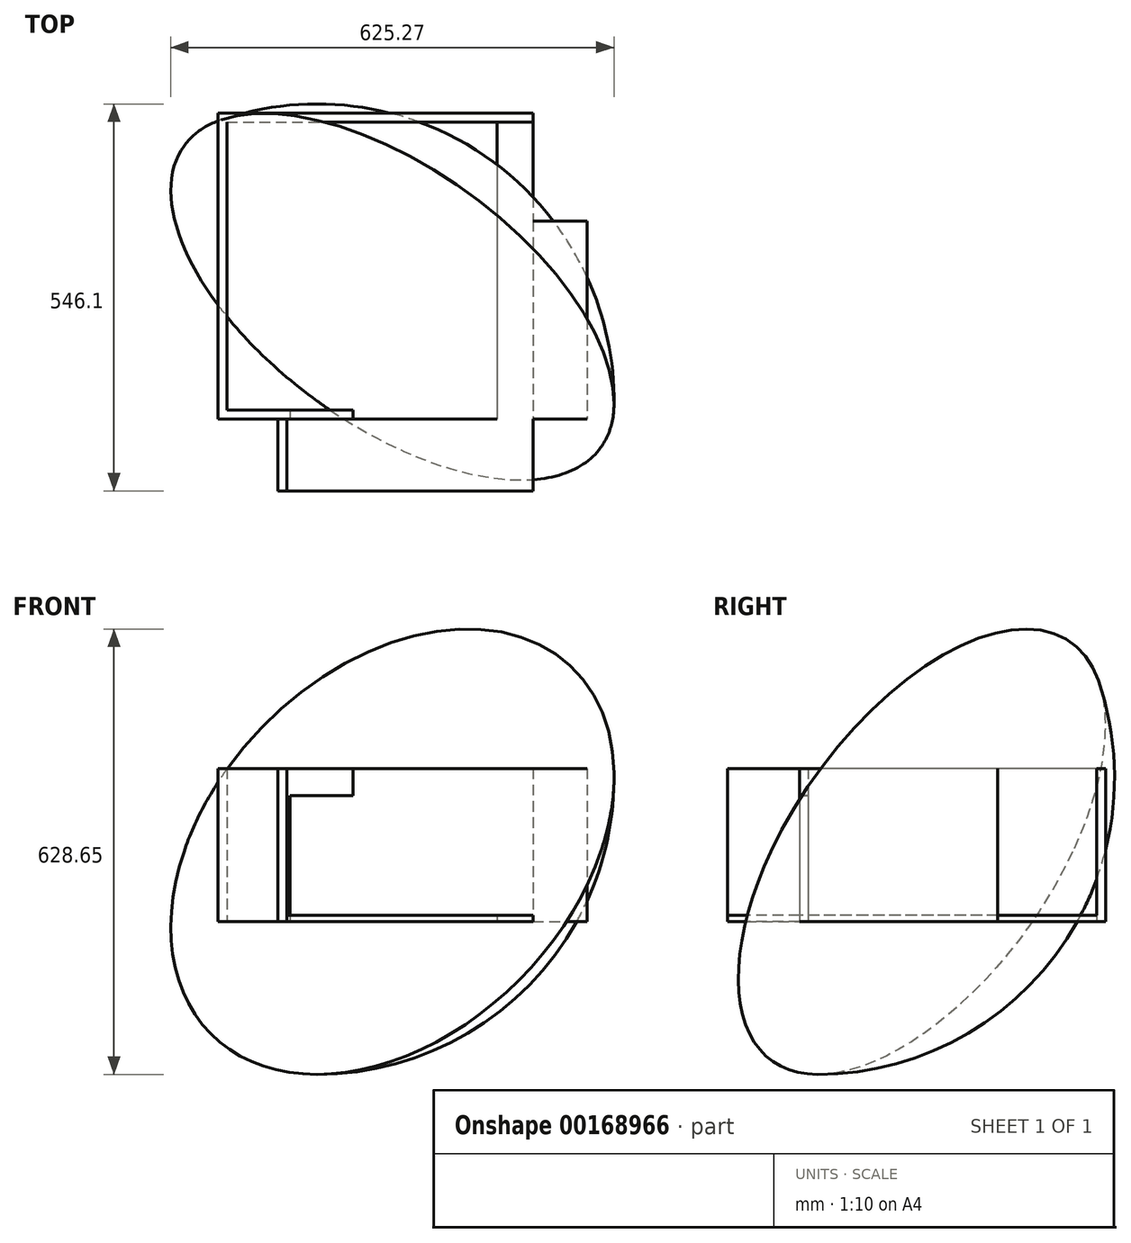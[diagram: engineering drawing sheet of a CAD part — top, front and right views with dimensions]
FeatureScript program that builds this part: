
annotation { "Feature Type Name" : "Feature", "Feature Type Description" : "" }
export const myFeature = defineFeature(function(context is Context, id is Id, definition is map)
    precondition{}
    {
        {
            var Q0;
            Q0=qCreatedBy(makeId("Top.planeOp"),FACE);
            var sketch = newSketch(context, id + "F0", { "sketchPlane" : qUnion([Q0])});
            skLineSegment(sketch, "E0.bottom", {"start": v(190.5, 209.55) * mm, "end": v(-190.5, 209.55) * mm});
            skLineSegment(sketch, "E0.top", {"start": v(190.5, -209.55) * mm, "end": v(-190.5, -209.55) * mm});
            skLineSegment(sketch, "E0.left", {"start": v(190.5, 209.55) * mm, "end": v(190.5, -209.55) * mm});
            skLineSegment(sketch, "E0.right", {"start": v(-190.5, 209.55) * mm, "end": v(-190.5, -209.55) * mm});
            skPoint(sketch, "E0.middle", {"position": v(0, 0) * mm});
            skLineSegment(sketch, "E1.bottom", {"start": v(190.5, 209.55) * mm, "end": v(241.3, 209.55) * mm});
            skLineSegment(sketch, "E1.top", {"start": v(190.5, -209.55) * mm, "end": v(241.3, -209.55) * mm});
            skLineSegment(sketch, "E1.right", {"start": v(241.3, 209.55) * mm, "end": v(241.3, -209.55) * mm});
            skLineSegment(sketch, "E2.top", {"start": v(190.5, 158.75) * mm, "end": v(-190.5, 158.75) * mm});
            skLineSegment(sketch, "E2.left", {"start": v(190.5, 209.55) * mm, "end": v(190.5, 158.75) * mm});
            skLineSegment(sketch, "E2.right", {"start": v(-190.5, 209.55) * mm, "end": v(-190.5, 158.75) * mm});
            skLineSegment(sketch, "E3.bottom", {"start": v(-190.5, -209.55) * mm, "end": v(-63.5, -209.55) * mm});
            skLineSegment(sketch, "E3.top", {"start": v(-190.5, 158.75) * mm, "end": v(-63.5, 158.75) * mm});
            skLineSegment(sketch, "E3.left", {"start": v(-190.5, -209.55) * mm, "end": v(-190.5, 158.75) * mm});
            skLineSegment(sketch, "E3.right", {"start": v(-63.5, -209.55) * mm, "end": v(-63.5, 158.75) * mm});
            skLineSegment(sketch, "E4.bottom", {"start": v(114.3, -209.55) * mm, "end": v(-63.5, -209.55) * mm});
            skLineSegment(sketch, "E4.top", {"start": v(114.3, -133.35) * mm, "end": v(-63.5, -133.35) * mm});
            skLineSegment(sketch, "E4.left", {"start": v(114.3, -209.55) * mm, "end": v(114.3, -133.35) * mm});
            skLineSegment(sketch, "E4.right", {"start": v(-63.5, -209.55) * mm, "end": v(-63.5, -133.35) * mm});
            skLineSegment(sketch, "E5.bottom", {"start": v(-190.5, -209.55) * mm, "end": v(-12.7, -209.55) * mm});
            skLineSegment(sketch, "E5.top", {"start": v(-190.5, -196.85) * mm, "end": v(-12.7, -196.85) * mm});
            skLineSegment(sketch, "E5.left", {"start": v(-190.5, -209.55) * mm, "end": v(-190.5, -196.85) * mm});
            skLineSegment(sketch, "E5.right", {"start": v(-12.7, -209.55) * mm, "end": v(-12.7, -196.85) * mm});
            skLineSegment(sketch, "E6.bottom", {"start": v(241.3, 69.85) * mm, "end": v(317.5, 69.85) * mm});
            skLineSegment(sketch, "E6.top", {"start": v(241.3, -209.55) * mm, "end": v(317.5, -209.55) * mm});
            skLineSegment(sketch, "E6.left", {"start": v(241.3, 69.85) * mm, "end": v(241.3, -209.55) * mm});
            skLineSegment(sketch, "E6.right", {"start": v(317.5, 69.85) * mm, "end": v(317.5, -209.55) * mm});
            skLineSegment(sketch, "E7", {"start": v(-59.05, 209.55) * mm, "end": v(-59.05, 196.85) * mm});
            skLineSegment(sketch, "E8", {"start": v(241.3, -107.95) * mm, "end": v(228.6, -107.95) * mm});
            skLineSegment(sketch, "E9", {"start": v(-59.05, 196.85) * mm, "end": v(228.6, -107.95) * mm});
            skArc(sketch, "E10", {"start": v(265.13, 309.56) * mm, "mid": v(-114.7, 132.44) * mm, "end": v(-151.23, -285.07) * mm, "construction": true});
            skLineSegment(sketch, "E11", {"start": v(228.6, -107.95) * mm, "end": v(-151.23, -285.07) * mm, "construction": true});
            skLineSegment(sketch, "E12", {"start": v(228.6, -107.95) * mm, "end": v(265.13, 309.56) * mm, "construction": true});
            skArc(sketch, "E13", {"start": v(-217.2, -191.26) * mm, "mid": v(197.99, -134.17) * mm, "end": v(356.14, 253.94) * mm, "construction": true});
            skLineSegment(sketch, "E14", {"start": v(-59.05, 196.85) * mm, "end": v(-217.2, -191.26) * mm, "construction": true});
            skLineSegment(sketch, "E15", {"start": v(-59.05, 196.85) * mm, "end": v(356.14, 253.94) * mm, "construction": true});
            skLineSegment(sketch, "E16", {"start": v(-63.5, -196.85) * mm, "end": v(-63.5, -184.15) * mm});
            skLineSegment(sketch, "E17", {"start": v(-63.5, -184.15) * mm, "end": v(189.23, 196.85) * mm});
            skPoint(sketch, "E17.endSnap0", {"position": v(190.5, 184.15) * mm});
            skLineSegment(sketch, "E18", {"start": v(189.23, 196.85) * mm, "end": v(189.23, 209.55) * mm});
            skArc(sketch, "E19", {"start": v(353.37, -227.35) * mm, "mid": v(182.35, 155.27) * mm, "end": v(-234.52, 198.47) * mm, "construction": true});
            skLineSegment(sketch, "E20", {"start": v(-63.5, -184.15) * mm, "end": v(-234.52, 198.47) * mm, "construction": true});
            skLineSegment(sketch, "E21", {"start": v(-63.5, -184.15) * mm, "end": v(353.37, -227.35) * mm, "construction": true});
            skArc(sketch, "E22", {"start": v(-223.5, 269.63) * mm, "mid": v(-70.56, -132.02) * mm, "end": v(355.58, -187.82) * mm, "construction": true});
            skLineSegment(sketch, "E23", {"start": v(189.23, 196.85) * mm, "end": v(332.57, -196.98) * mm, "construction": true});
            skLineSegment(sketch, "E24", {"start": v(189.23, 196.85) * mm, "end": v(-223.5, 269.63) * mm, "construction": true});
            skSolve(sketch);
        }
        {
            var Q0;
            Q0=qCreatedBy(makeId("Top.planeOp"),FACE);
            var sketch = newSketch(context, id + "F1", { "sketchPlane" : qUnion([Q0])});
            skLineSegment(sketch, "E25.0", {"start": v(190.5, 209.55) * mm, "end": v(241.3, 209.55) * mm});
            skLineSegment(sketch, "E26.0", {"start": v(190.5, 209.55) * mm, "end": v(-190.5, 209.55) * mm});
            skLineSegment(sketch, "E27.0", {"start": v(-190.5, 209.55) * mm, "end": v(-190.5, 158.75) * mm});
            skLineSegment(sketch, "E28.0", {"start": v(-190.5, 209.55) * mm, "end": v(-190.5, -197.06) * mm});
            skLineSegment(sketch, "E29.0", {"start": v(190.5, 222.25) * mm, "end": v(241.3, 222.25) * mm});
            skLineSegment(sketch, "E29.1", {"start": v(190.5, 222.25) * mm, "end": v(-203.2, 222.25) * mm});
            skLineSegment(sketch, "E29.2", {"start": v(-203.2, 222.25) * mm, "end": v(-203.2, -209.55) * mm});
            skLineSegment(sketch, "E30", {"start": v(241.3, 209.55) * mm, "end": v(241.3, 222.25) * mm});
            skLineSegment(sketch, "E31", {"start": v(-190.5, -209.55) * mm, "end": v(-203.2, -209.55) * mm});
            skLineSegment(sketch, "E32", {"start": v(-190.5, -197.06) * mm, "end": v(-101.6, -197.06) * mm});
            skLineSegment(sketch, "E33", {"start": v(-101.6, -197.06) * mm, "end": v(-101.6, -209.55) * mm});
            skLineSegment(sketch, "E34", {"start": v(-101.6, -209.55) * mm, "end": v(-190.5, -209.55) * mm});
            skLineSegment(sketch, "E35.0", {"start": v(241.3, 69.85) * mm, "end": v(317.5, 69.85) * mm});
            skLineSegment(sketch, "E36.0", {"start": v(317.5, 69.85) * mm, "end": v(317.5, -209.55) * mm});
            skLineSegment(sketch, "E37.0", {"start": v(241.3, -209.55) * mm, "end": v(317.5, -209.55) * mm});
            skLineSegment(sketch, "E38.0", {"start": v(241.3, 69.85) * mm, "end": v(241.3, -209.55) * mm});
            skPoint(sketch, "E39.orphan", {"position": v(241.3, 209.55) * mm});
            skSolve(sketch);
        }
        {
            var Q0;
            Q0=makeQuery(id+"F1.imprint","IMPRINT",FACE,{"disambiguationData":[TD([[makeQuery(id+"F1.imprint","IMPRINT",EDGE,{"derivedFrom":sQuery(id+"F1.wireOp",EDGE,"E25.0")}),1.0]])]});
            var Q1;
            {var subQ3=sQuery(id+"F0.wireOp",EDGE,"E6.bottom");Q1=makeQuery(id+"F0.imprint","IMPRINT",FACE,{"disambiguationData":[TD([[makeQuery(id+"F0.imprint","IMPRINT",EDGE,{"derivedFrom":subQ3}),-1.0]])]});}
            extrude(context, id + "F2", {"entities" : qUnion([Q0, Q1]), "depth" : 215.9 * mm});
        }
        {
            var Q0;
            Q0=makeQuery(id+"F2.opExtrude","CAP_FACE",FACE,{"disambiguationData":[OSD([sQuery(id+"F1.wireOp",EDGE,"E25.0"),sQuery(id+"F1.wireOp",EDGE,"E26.0"),sQuery(id+"F1.wireOp",EDGE,"E28.0"),sQuery(id+"F1.wireOp",EDGE,"E29.0"),sQuery(id+"F1.wireOp",EDGE,"E29.1"),sQuery(id+"F1.wireOp",EDGE,"E29.2"),sQuery(id+"F1.wireOp",EDGE,"E30"),sQuery(id+"F1.wireOp",EDGE,"E31"),sQuery(id+"F1.wireOp",EDGE,"E32"),sQuery(id+"F1.wireOp",EDGE,"E33"),sQuery(id+"F1.wireOp",EDGE,"E34")])],"isStart":false});
            var sketch = newSketch(context, id + "F3", { "sketchPlane" : qUnion([Q0])});
            skLineSegment(sketch, "E40.0", {"start": v(-12.7, -209.55) * mm, "end": v(-12.7, -196.85) * mm});
            skLineSegment(sketch, "E41.0", {"start": v(-12.7, -209.55) * mm, "end": v(-63.5, -209.55) * mm});
            skLineSegment(sketch, "E42.0", {"start": v(-101.6, -209.55) * mm, "end": v(-12.7, -209.55) * mm});
            skLineSegment(sketch, "E43.0", {"start": v(-101.6, -197.06) * mm, "end": v(-101.6, -209.55) * mm});
            skPoint(sketch, "E44.orphan", {"position": v(-190.5, -209.55) * mm});
            skPoint(sketch, "E45.0.end.orphan", {"position": v(-12.7, -196.85) * mm});
            skPoint(sketch, "E45.0.start.orphan", {"position": v(-190.5, -196.85) * mm});
            skPoint(sketch, "E46.orphan", {"position": v(114.3, -209.55) * mm});
            skLineSegment(sketch, "E47", {"start": v(-101.6, -197.06) * mm, "end": v(-12.7, -196.85) * mm});
            skSolve(sketch);
        }
        {
            var Q0;
            {var subQ0=sQuery(id+"F3.wireOp",EDGE,"E40.0");Q0=makeQuery(id+"F3.imprint","IMPRINT",FACE,{"disambiguationData":[TD([[makeQuery(id+"F3.imprint","IMPRINT",EDGE,{"derivedFrom":subQ0}),1.0]])]});}
            extrude(context, id + "F4", {"entities" : qUnion([Q0]), "operationType" : NewBodyOperationType.ADD, "oppositeDirection" : true, "depth" : 38.1 * mm});
        }
        {
            var Q0;
            Q0=qCreatedBy(makeId("Top.planeOp"),FACE);
            var sketch = newSketch(context, id + "F5", { "sketchPlane" : qUnion([Q0])});
            skLineSegment(sketch, "E48.0", {"start": v(190.5, 209.55) * mm, "end": v(241.3, 209.55) * mm});
            skLineSegment(sketch, "E49.0", {"start": v(190.5, -209.55) * mm, "end": v(241.3, -209.55) * mm});
            skLineSegment(sketch, "E50.0", {"start": v(190.5, 209.55) * mm, "end": v(190.5, -209.55) * mm});
            skLineSegment(sketch, "E51.0", {"start": v(241.3, 209.55) * mm, "end": v(241.3, -209.55) * mm});
            skLineSegment(sketch, "E52.bottom", {"start": v(241.3, -209.55) * mm, "end": v(-105.83, -209.55) * mm});
            skLineSegment(sketch, "E52.top", {"start": v(241.3, -311.15) * mm, "end": v(-105.83, -311.15) * mm});
            skLineSegment(sketch, "E52.left", {"start": v(241.3, -209.55) * mm, "end": v(241.3, -311.15) * mm});
            skLineSegment(sketch, "E52.right", {"start": v(-105.83, -209.55) * mm, "end": v(-105.83, -311.15) * mm});
            skSolve(sketch);
        }
        {
            var Q0;
            Q0=makeQuery(id+"F5.imprint","IMPRINT",FACE,{"disambiguationData":[TD([[makeQuery(id+"F5.imprint","IMPRINT",EDGE,{"derivedFrom":sQuery(id+"F5.wireOp",EDGE,"E52.top")}),-1.0]])]});
            var Q1;
            Q1=makeQuery(id+"F0.imprint","IMPRINT",FACE,{"disambiguationData":[TD([[makeQuery(id+"F0.imprint","IMPRINT",EDGE,{"derivedFrom":sQuery(id+"F0.wireOp",EDGE,"E1.bottom")}),-1.0]])]});
            var Q2;
            {var subQ2=sQuery(id+"F0.wireOp",EDGE,"E1.top");Q2=makeQuery(id+"F0.imprint","IMPRINT",FACE,{"disambiguationData":[TD([[makeQuery(id+"F0.imprint","IMPRINT",EDGE,{"derivedFrom":subQ2}),1.0]])]});}
            extrude(context, id + "F6", {"entities" : qUnion([Q0, Q1, Q2]), "operationType" : NewBodyOperationType.ADD, "depth" : 8.47 * mm});
        }
        {
            var Q0;
            Q0=qCreatedBy(makeId("Top.planeOp"),FACE);
            var sketch = newSketch(context, id + "F7", { "sketchPlane" : qUnion([Q0])});
            skLineSegment(sketch, "E53.0", {"start": v(-105.83, -209.55) * mm, "end": v(-105.83, -311.15) * mm});
            skLineSegment(sketch, "E54.bottom", {"start": v(-105.83, -311.15) * mm, "end": v(-118.53, -311.15) * mm});
            skLineSegment(sketch, "E54.top", {"start": v(-105.83, -209.55) * mm, "end": v(-118.53, -209.55) * mm});
            skLineSegment(sketch, "E54.left", {"start": v(-105.83, -311.15) * mm, "end": v(-105.83, -209.55) * mm});
            skLineSegment(sketch, "E54.right", {"start": v(-118.53, -311.15) * mm, "end": v(-118.53, -209.55) * mm});
            skSolve(sketch);
        }
        {
            var Q0;
            Q0=makeQuery(id+"F7.imprint","IMPRINT",FACE,{"disambiguationData":[TD([[makeQuery(id+"F7.imprint","IMPRINT",EDGE,{"derivedFrom":sQuery(id+"F7.wireOp",EDGE,"E54.bottom")}),-1.0]])]});
            extrude(context, id + "F8", {"entities" : qUnion([Q0]), "depth" : 215.9 * mm});
        }
        {
            var Q0;
            Q0=makeQuery(id+"F4.boolean.opBoolean","MERGE",FACE,{"derivedFrom":[makeQuery(id+"F2.opExtrude","CAP_FACE",FACE,{"disambiguationData":[OSD([sQuery(id+"F1.wireOp",EDGE,"E25.0"),sQuery(id+"F1.wireOp",EDGE,"E26.0"),sQuery(id+"F1.wireOp",EDGE,"E28.0"),sQuery(id+"F1.wireOp",EDGE,"E29.0"),sQuery(id+"F1.wireOp",EDGE,"E29.1"),sQuery(id+"F1.wireOp",EDGE,"E29.2"),sQuery(id+"F1.wireOp",EDGE,"E30"),sQuery(id+"F1.wireOp",EDGE,"E31"),sQuery(id+"F1.wireOp",EDGE,"E32"),sQuery(id+"F1.wireOp",EDGE,"E33"),sQuery(id+"F1.wireOp",EDGE,"E34")])],"isStart":false}),makeQuery(id+"F4.opExtrude","CAP_FACE",FACE,{"disambiguationData":[OSD([sQuery(id+"F3.wireOp",EDGE,"E40.0"),sQuery(id+"F3.wireOp",EDGE,"E42.0"),sQuery(id+"F3.wireOp",EDGE,"E43.0"),sQuery(id+"F3.wireOp",EDGE,"E47")])],"isStart":true})]});
            cPlane(context, id + "F9", {"entities" : qUnion([Q0]), "cplaneType" : CPlaneType.OFFSET, "offset" : 12.7 * mm, "oppositeDirection" : true, "width" : 152.4 * mm, "height" : 152.4 * mm});
        }
        {
            var Q0;
            Q0=qCreatedBy(id+"F9.planeOp",FACE);
            var sketch = newSketch(context, id + "F10", { "sketchPlane" : qUnion([Q0])});
            skLineSegment(sketch, "E55.0", {"start": v(-63.5, -184.15) * mm, "end": v(-234.52, 198.47) * mm});
            skLineSegment(sketch, "E56.0", {"start": v(-63.5, -184.15) * mm, "end": v(353.37, -227.35) * mm});
            skArc(sketch, "E57.0", {"start": v(353.37, -227.35) * mm, "mid": v(182.35, 155.27) * mm, "end": v(-234.52, 198.47) * mm});
            skArc(sketch, "E58.0", {"start": v(-223.5, 269.63) * mm, "mid": v(-80.17, -124.2) * mm, "end": v(332.57, -196.98) * mm});
            skLineSegment(sketch, "E59.0", {"start": v(189.23, 196.85) * mm, "end": v(-223.5, 269.63) * mm});
            skLineSegment(sketch, "E59.1", {"start": v(189.23, 196.85) * mm, "end": v(332.57, -196.98) * mm});
            skPoint(sketch, "E60.orphan", {"position": v(355.58, -187.82) * mm});
            skLineSegment(sketch, "E61", {"start": v(189.23, 196.85) * mm, "end": v(-80.17, -124.2) * mm});
            skLineSegment(sketch, "E62", {"start": v(-63.5, -184.15) * mm, "end": v(182.35, 155.27) * mm});
            skSolve(sketch);
        }
        {
            var Q0;
            Q0=sQuery(id+"F10.wireOp",EDGE,"E57.0");
            cPoint(context, id + "F11", {"entities" : qUnion([Q0]), "parameter" : 0.5});
        }
        {
            var Q0;
            Q0=sQuery(id+"F0.wireOp",VERTEX,"E20.start");
            var Q1;
            Q1=sQuery(id+"F10.wireOp",VERTEX,"E56.0.start");
            var Q2;
            Q2 = qCreatedBy(id + "F11" ,VERTEX);
            cPlane(context, id + "F12", {"entities" : qUnion([Q0, Q1, Q2]), "cplaneType" : CPlaneType.THREE_POINT, "offset" : 0 * mm, "width" : 152.4 * mm, "height" : 152.4 * mm});
        }
        {
            var Q0;
            Q0=qCreatedBy(id+"F12.planeOp",FACE);
            var sketch = newSketch(context, id + "F13", { "sketchPlane" : qUnion([Q0])});
            skPoint(sketch, "E63.0", {"position": v(-186.39, 203.2) * mm});
            skLineSegment(sketch, "E64.0", {"start": v(-186.39, 203.2) * mm, "end": v(232.71, 203.2) * mm});
            skLineSegment(sketch, "E65", {"start": v(-186.39, 203.2) * mm, "end": v(-186.39, -215.9) * mm});
            skArc(sketch, "E66", {"start": v(-186.39, -215.9) * mm, "mid": v(176.56, -6.35) * mm, "end": v(176.56, 412.75) * mm});
            skLineSegment(sketch, "E67", {"start": v(-186.39, 203.2) * mm, "end": v(176.56, 412.75) * mm});
            skLineSegment(sketch, "E68", {"start": v(-186.39, 203.2) * mm, "end": v(176.56, -6.35) * mm});
            skSolve(sketch);
        }
        {
            var Q0;
            {var subQ0=sQuery(id+"F13.wireOp",EDGE,"E65");Q0=makeQuery(id+"F13.imprint","IMPRINT",FACE,{"disambiguationData":[TD([[makeQuery(id+"F13.imprint","IMPRINT",EDGE,{"derivedFrom":subQ0}),1.0]])]});}
            var Q1;
            Q1=sQuery(id+"F13.wireOp",EDGE,"E68");
            revolve(context, id + "F14", {"entities" : qUnion([Q0]), "axis" : qUnion([Q1]), "revolveType" : RevolveType.FULL});
        }
    });
